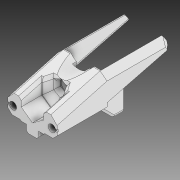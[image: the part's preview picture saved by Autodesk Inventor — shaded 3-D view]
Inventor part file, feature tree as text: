
AUTODESK INVENTOR PART (.ipt)
format: ipt  version: 2020 (Build 240168000, 168)  size: 270,848 bytes
history: native  units: in
note: dims shown in document units (in); Inventor stores cm internally (conversion verified against a paired STEP export)
features: extrude x2, sketch x2, fillet x1, chamfer x1, imported_body x1
ambient origin geometry x8: Origin, YZ Plane, XZ Plane, XY Plane, X Axis, Y Axis, Z Axis, Center Point
bodies: Solid1 (feature_tree)
feature tree (7):
  extrude  "Extrusion1"  TaperAngle=0.0deg  [1 undecoded]
  fillet  "Fillet1"  Radius=0.0787in
  extrude  "Extrusion2"  Depth=0.0591in TaperAngle=45.0deg
  chamfer  "Chamfer1"  [1 undecoded]
  sketch  "Sketch1"  dims[d0=0.9843in d1=0.0in d2=0.0in d3=0.0787in]
  sketch  "Sketch2"  dims[d4=0.0in d5=0.0in d6=0.0591in d7=0.0787in d8=45.0deg]
  imported_body  "Base1"
note: 2 required parameter values undecoded (feature->parameter linkage not recoverable at this tier; creation-order binding heuristic only, values carry confidence <= 0.55)
